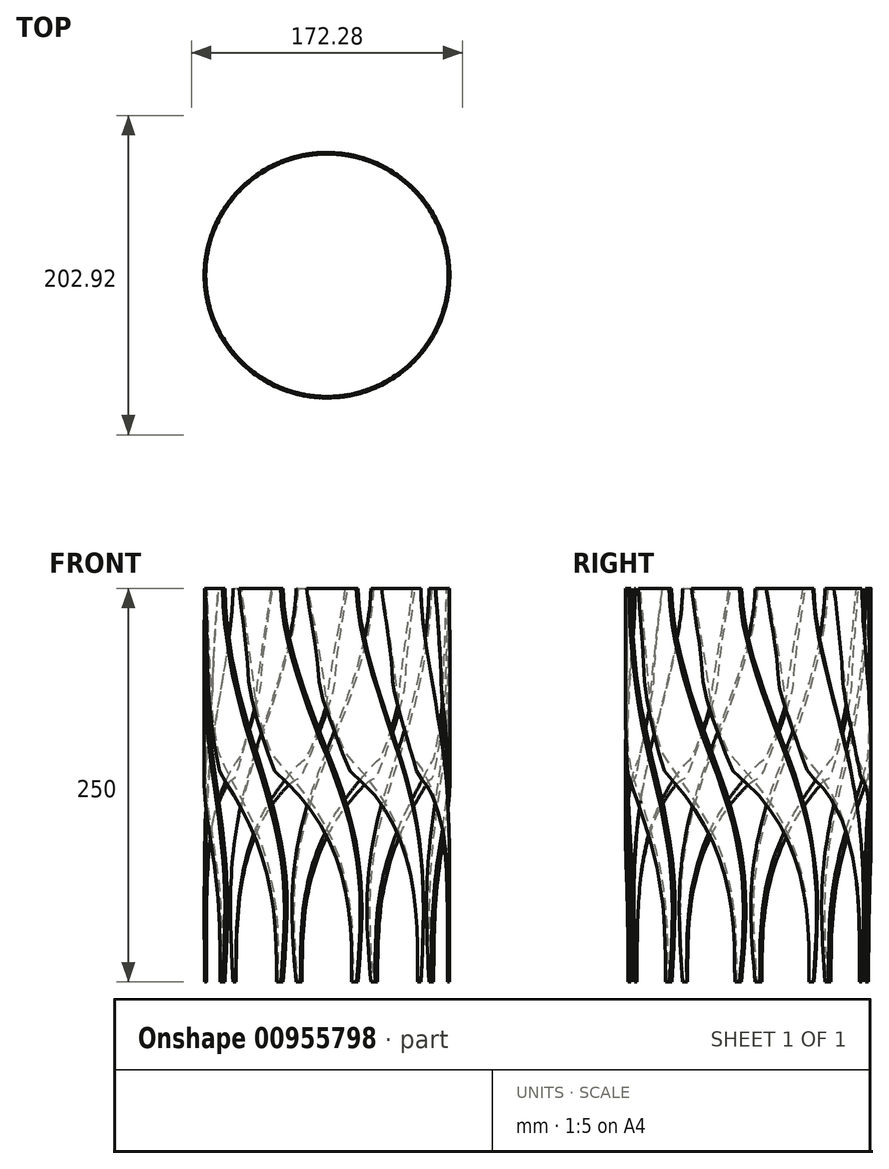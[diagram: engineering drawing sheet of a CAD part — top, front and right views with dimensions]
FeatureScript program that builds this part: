
annotation { "Feature Type Name" : "Feature", "Feature Type Description" : "" }
export const myFeature = defineFeature(function(context is Context, id is Id, definition is map)
    precondition{}
    {
        {
            var Q0;
            Q0=qCreatedBy(makeId("Top.planeOp"),FACE);
            var sketch = newSketch(context, id + "F0", { "sketchPlane" : qUnion([Q0])});
            skCircle(sketch, "E0", {"center": v(0, 0) * mm, "radius": 105 * mm, "construction": true});
            skCircle(sketch, "E1", {"center": v(0, 0) * mm, "radius": 50 * mm, "construction": true});
            skArc(sketch, "E2", {"start": v(86.63, 59.33) * mm, "mid": v(41.73, 72.89) * mm, "end": v(0.8, 50) * mm});
            skArc(sketch, "E3.0", {"start": v(87.91, 60.86) * mm, "mid": v(41.51, 74.88) * mm, "end": v(-0.8, 51.22) * mm});
            skArc(sketch, "E4", {"start": v(86.63, 59.33) * mm, "mid": v(88.04, 59.45) * mm, "end": v(87.91, 60.86) * mm});
            skArc(sketch, "E5", {"start": v(-0.8, 51.22) * mm, "mid": v(-0.61, 49.82) * mm, "end": v(0.8, 50) * mm});
            skSolve(sketch);
        }
        {
            var Q0;
            Q0=qCreatedBy(makeId("Top.planeOp"),FACE);
            cPlane(context, id + "F1", {"entities" : qUnion([Q0]), "cplaneType" : CPlaneType.OFFSET, "offset" : 250 * mm, "width" : 150 * mm, "height" : 150 * mm});
        }
        {
            var Q0;
            Q0=qCreatedBy(id+"F1.planeOp",FACE);
            var sketch = newSketch(context, id + "F2", { "sketchPlane" : qUnion([Q0])});
            skCircle(sketch, "E6", {"center": v(0, 0) * mm, "radius": 90 * mm, "construction": true});
            skCircle(sketch, "E7", {"center": v(0, 0) * mm, "radius": 50 * mm, "construction": true});
            skArc(sketch, "E8", {"start": v(89.87, -4.78) * mm, "mid": v(70.1, 16.7) * mm, "end": v(42.52, 26.31) * mm});
            skArc(sketch, "E9.0", {"start": v(107.44, 4.78) * mm, "mid": v(81.07, 33.43) * mm, "end": v(44.3, 46.23) * mm});
            skArc(sketch, "E10", {"start": v(89.87, -4.78) * mm, "mid": v(103.44, -8.78) * mm, "end": v(107.44, 4.78) * mm});
            skArc(sketch, "E11", {"start": v(44.3, 46.23) * mm, "mid": v(33.45, 37.17) * mm, "end": v(42.52, 26.31) * mm});
            skSolve(sketch);
        }
        {
            var Q0;
            Q0=sQuery(id+"F2.wireOp",VERTEX,"E10.center");
            var Q1;
            Q1=sQuery(id+"F0.wireOp",VERTEX,"E4.center");
            var Q2;
            Q2=sQuery(id+"F2.wireOp",VERTEX,"E11.center");
            cPlane(context, id + "F3", {"entities" : qUnion([Q0, Q1, Q2]), "cplaneType" : CPlaneType.THREE_POINT, "offset" : 25 * mm, "width" : 150 * mm, "height" : 150 * mm});
        }
        {
            var Q0;
            Q0=qCreatedBy(id+"F3.planeOp",FACE);
            var sketch = newSketch(context, id + "F4", { "sketchPlane" : qUnion([Q0])});
            skFitSpline(sketch, "E12", {"points": [v(55.17, 244.64) * mm, v(41.64, -12.38) * mm], "startDerivative": vector(-127.45, -376) * mm, "endDerivative": vector(85.82, -280.84) * mm});
            skSolve(sketch);
        }
        {
            var Q0;
            Q0 = qConstructionFilter(qBodyType(qCreatedBy(id + "F4" ,EDGE), BodyType.WIRE), ConstructionObject.NO);
            var Q1;
            Q1=makeQuery(id+"F0.imprint","IMPRINT",FACE,{"disambiguationData":[TD([[makeQuery(id+"F0.imprint","IMPRINT",EDGE,{"derivedFrom":sQuery(id+"F0.wireOp",EDGE,"E2")}),-1.0]])]});
            var Q2;
            Q2=makeQuery(id+"F2.imprint","IMPRINT",FACE,{"disambiguationData":[TD([[makeQuery(id+"F2.imprint","IMPRINT",EDGE,{"derivedFrom":sQuery(id+"F2.wireOp",EDGE,"E8")}),-1.0]])]});
            loft(context, id + "F5", {"addSections" : true, "spine" : qUnion([Q0]), "sectionCount" : 5, "sheetProfilesArray" : [{ "sheetProfileEntities" : qUnion([Q1]) }, { "sheetProfileEntities" : qUnion([Q2]) }]});
        }
        {
            var Q0;
            Q0=qCreatedBy(makeId("Right.planeOp"),FACE);
            var sketch = newSketch(context, id + "F6", { "sketchPlane" : qUnion([Q0])});
            skLineSegment(sketch, "E13", {"start": v(0, 0) * mm, "end": v(0, 65.3) * mm, "construction": true});
            skSolve(sketch);
        }
        {
            var Q0;
            Q0=makeQuery(id+"F5.opLoft","SWEPT_BODY",BODY,{"disambiguationData":[OSD([makeQuery(id+"F0.imprint","IMPRINT",FACE,{"disambiguationData":[TD([[makeQuery(id+"F0.imprint","IMPRINT",EDGE,{"derivedFrom":sQuery(id+"F0.wireOp",EDGE,"E2")}),-1.0]])]}),makeQuery(id+"F2.imprint","IMPRINT",FACE,{"disambiguationData":[TD([[makeQuery(id+"F2.imprint","IMPRINT",EDGE,{"derivedFrom":sQuery(id+"F2.wireOp",EDGE,"E8")}),-1.0]])]})])]});
            var Q1;
            Q1=sQuery(id+"F6.wireOp",EDGE,"E13");
            circularPattern(context, id + "F7", {"entities" : qUnion([Q0]), "axis" : qUnion([Q1]), "angle" : 360 * degree, "instanceCount" : 10, "equalSpace" : true});
        }
        {
            var Q0;
            Q0=makeQuery(id+"F5.opLoft","CAP_FACE",FACE,{"disambiguationData":[OSD([makeQuery(id+"F2.imprint","IMPRINT",FACE,{"disambiguationData":[TD([[makeQuery(id+"F2.imprint","IMPRINT",EDGE,{"derivedFrom":sQuery(id+"F2.wireOp",EDGE,"E8")}),-1.0]])]})])],"isStart":true});
            var sketch = newSketch(context, id + "F8", { "sketchPlane" : qUnion([Q0])});
            skCircle(sketch, "E14", {"center": v(0, 0) * mm, "radius": 108.66 * mm});
            skSolve(sketch);
        }
        {
            var Q0;
            Q0=makeQuery(id+"F7.opPattern","COPY",FACE,{"derivedFrom":makeQuery(id+"F5.opLoft","CAP_FACE",FACE,{"disambiguationData":[OSD([makeQuery(id+"F2.imprint","IMPRINT",FACE,{"disambiguationData":[TD([[makeQuery(id+"F2.imprint","IMPRINT",EDGE,{"derivedFrom":sQuery(id+"F2.wireOp",EDGE,"E8")}),-1.0]])]})])],"isStart":true}),"instanceName":"5"});
            var sketch = newSketch(context, id + "F9", { "sketchPlane" : qUnion([Q0])});
            skCircle(sketch, "E15.0", {"center": v(0, 0) * mm, "radius": 65 * mm});
            skCircle(sketch, "E16", {"center": v(0, 0) * mm, "radius": 21 * mm});
            skSolve(sketch);
        }
        {
            var Q0;
            Q0 = qSketchRegion(id + "F9", true);
            extrude(context, id + "F10", {"entities" : qUnion([Q0]), "operationType" : NewBodyOperationType.ADD, "oppositeDirection" : true, "depth" : 40 * mm, "offsetDistance" : 25 * mm, "hasSecondDirection" : true, "secondDirectionOppositeDirection" : true, "secondDirectionDepth" : 35 * mm});
        }
        {
            var Q0;
            Q0=qCreatedBy(makeId("Front.planeOp"),FACE);
            var sketch = newSketch(context, id + "F11", { "sketchPlane" : qUnion([Q0])});
            skLineSegment(sketch, "E17", {"start": v(0, 0) * mm, "end": v(0, 300.26) * mm, "construction": true});
            skLineSegment(sketch, "E18.bottom", {"start": v(78, 0) * mm, "end": v(77, 0) * mm});
            skLineSegment(sketch, "E18.top", {"start": v(78, 250) * mm, "end": v(77, 250) * mm});
            skLineSegment(sketch, "E18.left", {"start": v(78, 0) * mm, "end": v(78, 250) * mm});
            skLineSegment(sketch, "E18.right", {"start": v(77, 0) * mm, "end": v(77, 250) * mm});
            skSolve(sketch);
        }
        {
            var Q0;
            Q0=qCreatedBy(makeId("Top.planeOp"),FACE);
            var sketch = newSketch(context, id + "F12", { "sketchPlane" : qUnion([Q0])});
            skCircle(sketch, "E19", {"center": v(0, 0) * mm, "radius": 17.5 * mm});
            skLineSegment(sketch, "E20", {"start": v(0, 17.5) * mm, "end": v(0, -17.5) * mm});
            skSolve(sketch);
        }
        {
            var Q0;
            {var subQ0=sQuery(id+"F12.wireOp",EDGE,"E20");Q0=makeQuery(id+"F12.imprint","IMPRINT",FACE,{"disambiguationData":[TD([[makeQuery(id+"F12.imprint","IMPRINT",EDGE,{"derivedFrom":subQ0}),1.0]])]});}
            var Q1;
            Q1=makeQuery(id+"F7.opPattern","COPY",FACE,{"derivedFrom":makeQuery(id+"F5.opLoft","CAP_FACE",FACE,{"disambiguationData":[OSD([makeQuery(id+"F2.imprint","IMPRINT",FACE,{"disambiguationData":[TD([[makeQuery(id+"F2.imprint","IMPRINT",EDGE,{"derivedFrom":sQuery(id+"F2.wireOp",EDGE,"E8")}),-1.0]])]})])],"isStart":true}),"instanceName":"1"});
            extrude(context, id + "F13", {"entities" : qUnion([Q0]), "endBound" : BoundingType.UP_TO_SURFACE, "depth" : 25 * mm, "endBoundEntityFace" : qUnion([Q1]), "offsetDistance" : 25 * mm});
        }
        {
            var Q0;
            Q0 = qSketchRegion(id + "F11", true);
            var Q1;
            Q1=sQuery(id+"F11.wireOp",EDGE,"E17");
            revolve(context, id + "F14", {"operationType" : NewBodyOperationType.INTERSECT, "surfaceOperationType" : NewSurfaceOperationType.NEW, "entities" : qUnion([Q0]), "axis" : qUnion([Q1]), "revolveType" : RevolveType.FULL});
        }
    });
